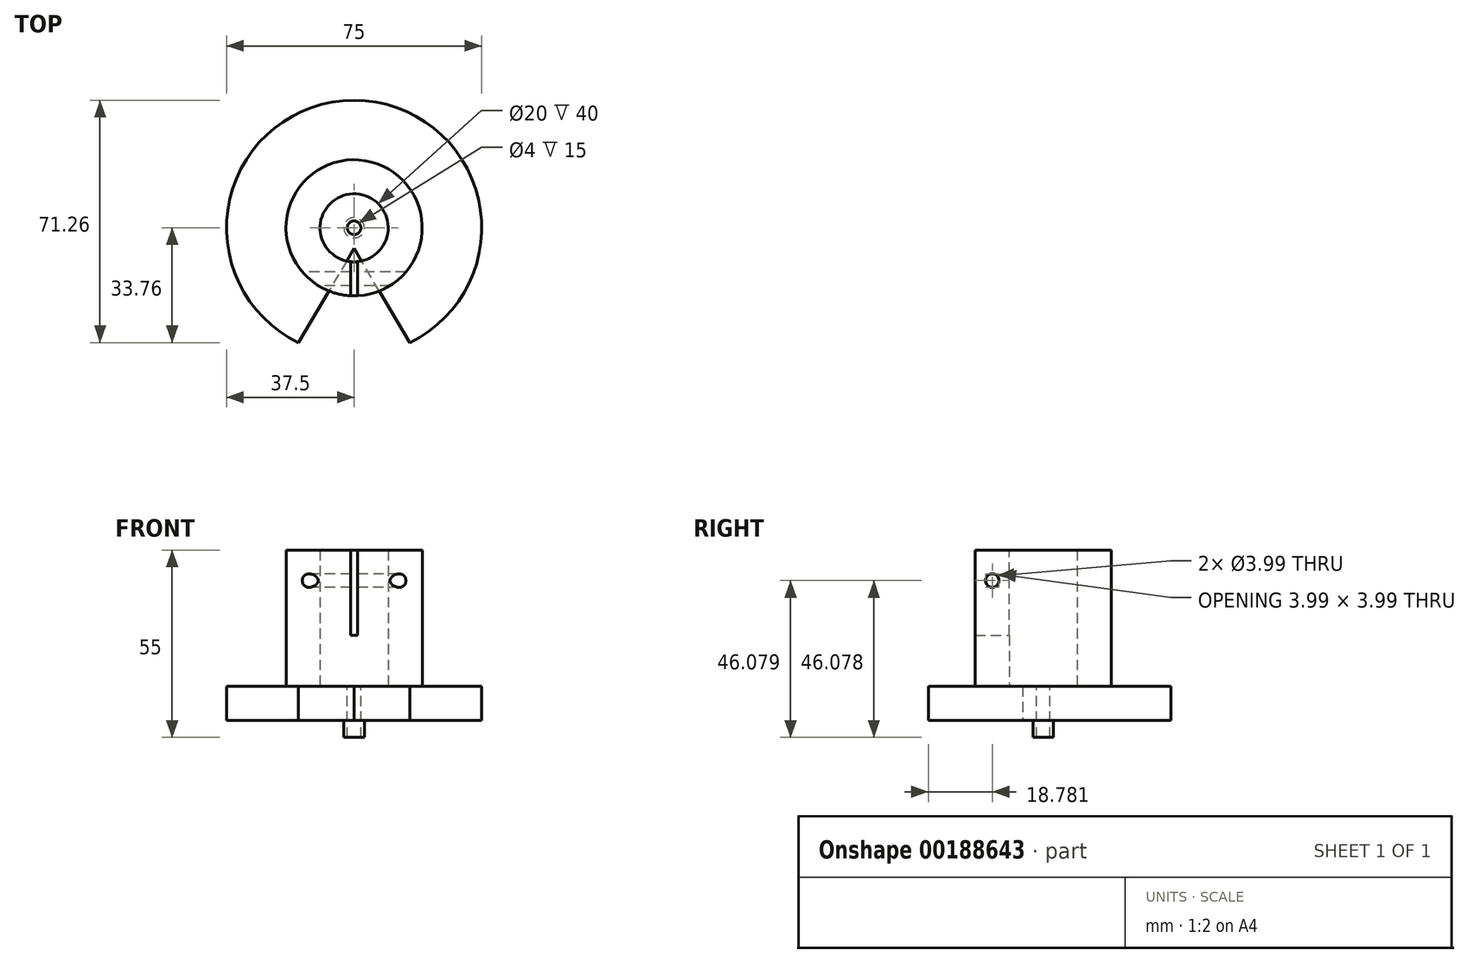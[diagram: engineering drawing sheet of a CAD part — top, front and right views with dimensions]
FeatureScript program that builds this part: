
annotation { "Feature Type Name" : "Feature", "Feature Type Description" : "" }
export const myFeature = defineFeature(function(context is Context, id is Id, definition is map)
    precondition{}
    {
        {
            var Q0;
            Q0=qCreatedBy(makeId("Top.planeOp"),FACE);
            var sketch = newSketch(context, id + "F0", { "sketchPlane" : qUnion([Q0])});
            skArc(sketch, "E0", {"start": v(16.33, -33.76) * mm, "mid": v(0, 37.5) * mm, "end": v(-16.33, -33.76) * mm});
            skCircle(sketch, "E1", {"center": v(0, 0) * mm, "radius": 3 * mm});
            skLineSegment(sketch, "E2", {"start": v(0, -6) * mm, "end": v(-16.33, -33.76) * mm});
            skLineSegment(sketch, "E3", {"start": v(16.33, -33.76) * mm, "end": v(0, -6) * mm});
            skSolve(sketch);
        }
        {
            var Q0;
            Q0=makeQuery(id+"F0.imprint","IMPRINT",FACE,{"disambiguationData":[TD([[makeQuery(id+"F0.imprint","IMPRINT",EDGE,{"derivedFrom":sQuery(id+"F0.wireOp",EDGE,"E0")}),1.0]])]});
            extrude(context, id + "F1", {"entities" : qUnion([Q0]), "depth" : 10 * mm});
        }
        {
            var Q0;
            Q0=makeQuery(id+"F1.opExtrude","CAP_FACE",FACE,{"disambiguationData":[OSD([sQuery(id+"F0.wireOp",EDGE,"E0"),sQuery(id+"F0.wireOp",EDGE,"E1")])],"isStart":false});
            var sketch = newSketch(context, id + "F2", { "sketchPlane" : qUnion([Q0])});
            skCircle(sketch, "E4", {"center": v(0, 0) * mm, "radius": 20 * mm});
            skCircle(sketch, "E5", {"center": v(0, 0) * mm, "radius": 10 * mm});
            skSolve(sketch);
        }
        {
            var Q0;
            Q0=makeQuery(id+"F2.imprint","IMPRINT",FACE,{"disambiguationData":[TD([[makeQuery(id+"F2.imprint","IMPRINT",EDGE,{"derivedFrom":sQuery(id+"F2.wireOp",EDGE,"E4")}),1.0]])]});
            extrude(context, id + "F3", {"entities" : qUnion([Q0]), "operationType" : NewBodyOperationType.ADD, "depth" : 40 * mm});
        }
        {
            var Q0;
            Q0=makeQuery(id+"F3.opExtrude","CAP_FACE",FACE,{"disambiguationData":[OSD([sQuery(id+"F2.wireOp",EDGE,"E4"),sQuery(id+"F2.wireOp",EDGE,"E5")])],"isStart":false});
            var sketch = newSketch(context, id + "F4", { "sketchPlane" : qUnion([Q0])});
            skLineSegment(sketch, "E6.bottom", {"start": v(1, -23.93) * mm, "end": v(-1, -23.93) * mm});
            skLineSegment(sketch, "E6.top", {"start": v(1, -6.6) * mm, "end": v(-1, -6.6) * mm});
            skLineSegment(sketch, "E6.left", {"start": v(1, -23.93) * mm, "end": v(1, -6.6) * mm});
            skLineSegment(sketch, "E6.right", {"start": v(-1, -23.93) * mm, "end": v(-1, -6.6) * mm});
            skPoint(sketch, "E6.middle", {"position": v(0, -15.27) * mm});
            skSolve(sketch);
        }
        {
            var Q0;
            {var subQ0=sQuery(id+"F4.wireOp",EDGE,"E6.left");var subQ1=makeQuery(id+"F3.opExtrude","CAP_EDGE",EDGE,{"disambiguationData":[OSD([sQuery(id+"F2.wireOp",EDGE,"E4")])],"isStart":false});var subQ2=makeQuery(id+"F4.imprint","INTERSECT",VERTEX,{"derivedFrom":[subQ1,subQ0]});Q0=makeQuery(id+"F4.imprint","IMPRINT",FACE,{"disambiguationData":[TD([[makeQuery(id+"F4.imprint","IMPRINT",EDGE,{"disambiguationData":[TD([[subQ2,-1.0]])],"derivedFrom":subQ0}),1.0]])]});}
            extrude(context, id + "F5", {"entities" : qUnion([Q0]), "operationType" : NewBodyOperationType.REMOVE, "oppositeDirection" : true, "depth" : 25 * mm});
        }
        {
            var Q0;
            {var subQ1=sQuery(id+"F0.wireOp",EDGE,"E2");var subQ2=sQuery(id+"F0.wireOp",EDGE,"E3");var subQ3=sQuery(id+"F0.wireOp",EDGE,"E1");Q0=makeQuery(id+"F3.boolean.opBoolean","SPLIT",FACE,{"disambiguationData":[TD([makeQuery(id+"F1.opExtrude","SWEPT_FACE",FACE,{"disambiguationData":[OSD([subQ3])]})])],"derivedFrom":makeQuery(id+"F1.opExtrude","CAP_FACE",FACE,{"disambiguationData":[OSD([sQuery(id+"F0.wireOp",EDGE,"E0"),subQ3,subQ1,subQ2])],"isStart":false})});}
            var sketch = newSketch(context, id + "F6", { "sketchPlane" : qUnion([Q0])});
            skCircle(sketch, "E7", {"center": v(0, 0) * mm, "radius": 3 * mm});
            skCircle(sketch, "E8", {"center": v(0, 0) * mm, "radius": 2 * mm});
            skSolve(sketch);
        }
        {
            var Q0;
            Q0=makeQuery(id+"F6.imprint","IMPRINT",FACE,{"disambiguationData":[TD([[makeQuery(id+"F6.imprint","IMPRINT",EDGE,{"derivedFrom":sQuery(id+"F6.wireOp",EDGE,"E7")}),1.0]])]});
            extrude(context, id + "F7", {"entities" : qUnion([Q0]), "operationType" : NewBodyOperationType.ADD, "oppositeDirection" : true, "depth" : 15 * mm});
        }
        {
            var Q0;
            Q0=qCreatedBy(makeId("Right.planeOp"),FACE);
            var sketch = newSketch(context, id + "F8", { "sketchPlane" : qUnion([Q0])});
            skCircle(sketch, "E9", {"center": v(-14.98, 41.08) * mm, "radius": 2 * mm});
            skSolve(sketch);
        }
        {
            var Q0;
            Q0=makeQuery(id+"F8.imprint","IMPRINT",FACE,{"disambiguationData":[TD([[makeQuery(id+"F8.imprint","IMPRINT",EDGE,{"derivedFrom":sQuery(id+"F8.wireOp",EDGE,"E9")}),1.0]])]});
            extrude(context, id + "F9", {"entities" : qUnion([Q0]), "operationType" : NewBodyOperationType.REMOVE, "endBound" : BoundingType.SYMMETRIC, "depth" : 39 * mm});
        }
    });
